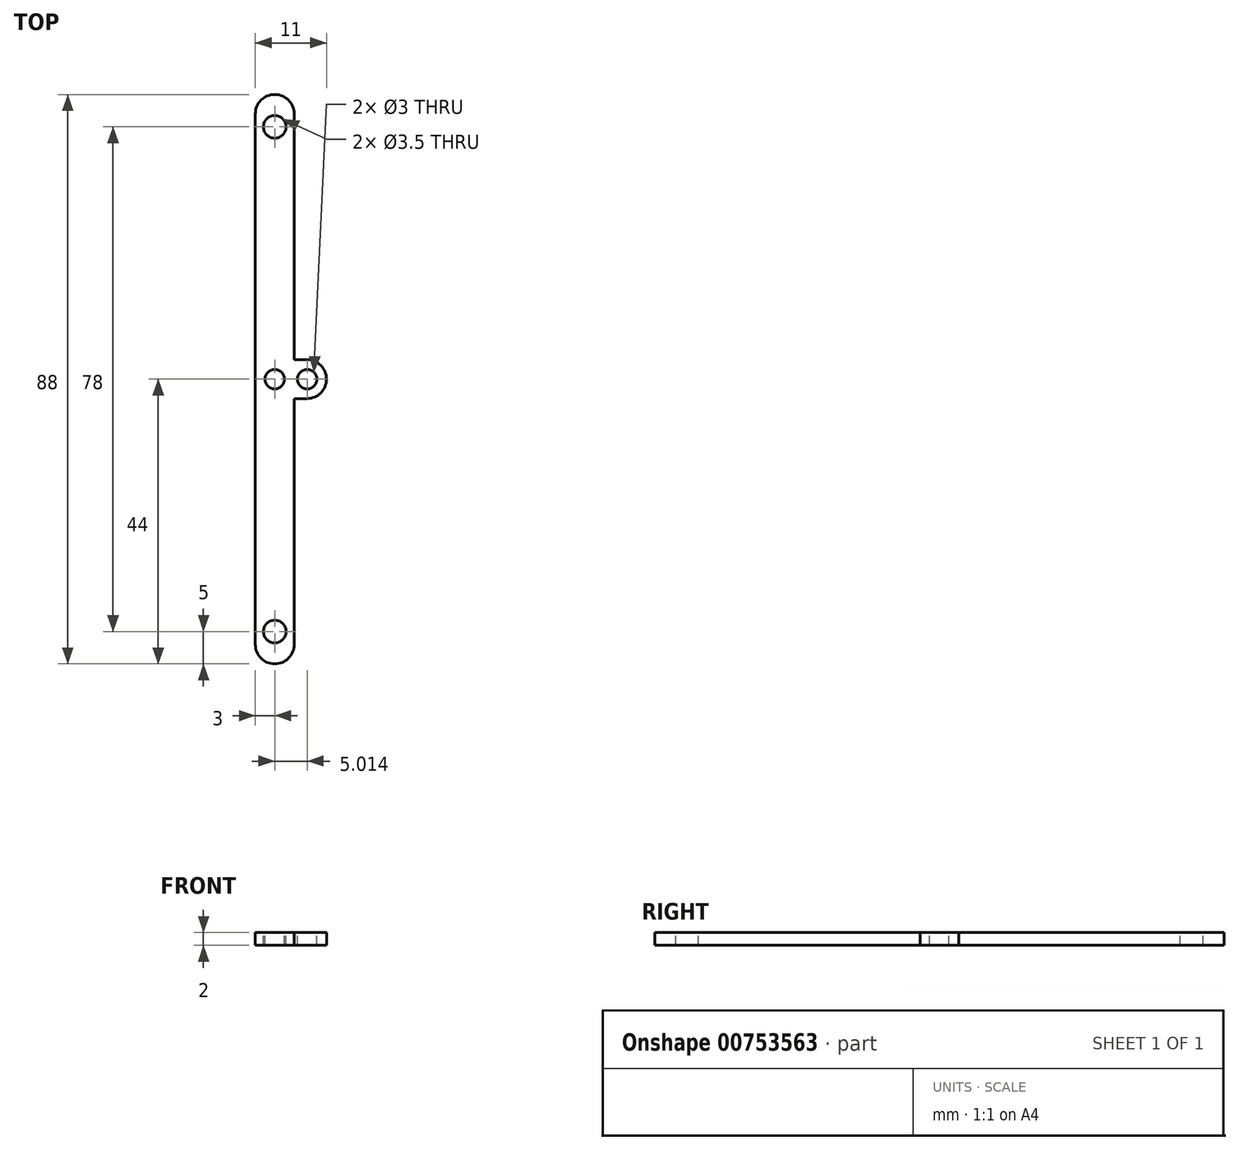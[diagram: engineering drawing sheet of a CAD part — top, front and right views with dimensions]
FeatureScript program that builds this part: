
annotation { "Feature Type Name" : "Feature", "Feature Type Description" : "" }
export const myFeature = defineFeature(function(context is Context, id is Id, definition is map)
    precondition{}
    {
        {
            var Q0;
            Q0=qCreatedBy(makeId("Top.planeOp"),FACE);
            var sketch = newSketch(context, id + "F0", { "sketchPlane" : qUnion([Q0])});
            skLineSegment(sketch, "E0.bottom", {"start": v(-3, 44) * mm, "end": v(3, 44) * mm});
            skLineSegment(sketch, "E0.top", {"start": v(-3, -44) * mm, "end": v(3, -44) * mm});
            skLineSegment(sketch, "E0.left", {"start": v(-3, 44) * mm, "end": v(-3, -44) * mm});
            skLineSegment(sketch, "E0.right", {"start": v(3, 44) * mm, "end": v(3, -44) * mm});
            skPoint(sketch, "E0.middle", {"position": v(0, 0) * mm});
            skSolve(sketch);
        }
        {
            var Q0;
            Q0 = qSketchRegion(id + "F0", true);
            extrude(context, id + "F1", {"entities" : qUnion([Q0]), "depth" : 2 * mm, "offsetDistance" : 25 * mm});
        }
        {
            var Q0;
            Q0=makeQuery(id+"F1.opExtrude","CAP_FACE",FACE,{"disambiguationData":[OSD([sQuery(id+"F0.wireOp",EDGE,"E0.bottom"),sQuery(id+"F0.wireOp",EDGE,"E0.top"),sQuery(id+"F0.wireOp",EDGE,"E0.left"),sQuery(id+"F0.wireOp",EDGE,"E0.right")])],"isStart":false});
            var sketch = newSketch(context, id + "F2", { "sketchPlane" : qUnion([Q0])});
            skCircle(sketch, "E1", {"center": v(0, 0) * mm, "radius": 1.5 * mm});
            skCircle(sketch, "E2", {"center": v(0, 39) * mm, "radius": 1.75 * mm});
            skCircle(sketch, "E3.MirrorC", {"center": v(0, -39) * mm, "radius": 1.75 * mm});
            skLineSegment(sketch, "E4", {"start": v(0, 39) * mm, "end": v(0, 44) * mm});
            skLineSegment(sketch, "E5", {"start": v(0, -44) * mm, "end": v(0, -39) * mm});
            skSolve(sketch);
        }
        {
            var Q0;
            Q0 = qSketchRegion(id + "F2", true);
            extrude(context, id + "F3", {"entities" : qUnion([Q0]), "operationType" : NewBodyOperationType.REMOVE, "endBound" : BoundingType.UP_TO_NEXT, "oppositeDirection" : true, "depth" : 25 * mm, "offsetDistance" : 25 * mm});
        }
        {
            var Q0;
            Q0=makeQuery(id+"F1.opExtrude","SWEPT_FACE",FACE,{"disambiguationData":[OSD([sQuery(id+"F0.wireOp",EDGE,"E0.right")])]});
            var sketch = newSketch(context, id + "F4", { "sketchPlane" : qUnion([Q0])});
            skLineSegment(sketch, "E6.bottom", {"start": v(0, 2) * mm, "end": v(3, 2) * mm});
            skLineSegment(sketch, "E6.top", {"start": v(0, 0) * mm, "end": v(3, 0) * mm});
            skLineSegment(sketch, "E6.right", {"start": v(3, 2) * mm, "end": v(3, 0) * mm});
            skLineSegment(sketch, "E7", {"start": v(0, 2) * mm, "end": v(-3, 2) * mm});
            skLineSegment(sketch, "E8", {"start": v(-3, 2) * mm, "end": v(-3, 0) * mm});
            skLineSegment(sketch, "E9", {"start": v(-3, 0) * mm, "end": v(0, 0) * mm});
            skSolve(sketch);
        }
        {
            var Q0;
            Q0 = qSketchRegion(id + "F4", true);
            extrude(context, id + "F5", {"entities" : qUnion([Q0]), "operationType" : NewBodyOperationType.ADD, "depth" : 5 * mm, "offsetDistance" : 25 * mm});
        }
        {
            var Q0;
            Q0=makeQuery(id+"F5.boolean.opBoolean","MERGE",FACE,{"derivedFrom":[makeQuery(id+"F1.opExtrude","CAP_FACE",FACE,{"disambiguationData":[OSD([sQuery(id+"F0.wireOp",EDGE,"E0.bottom"),sQuery(id+"F0.wireOp",EDGE,"E0.top"),sQuery(id+"F0.wireOp",EDGE,"E0.left"),sQuery(id+"F0.wireOp",EDGE,"E0.right")])],"isStart":false}),makeQuery(id+"F5.opExtrude","SWEPT_FACE",FACE,{"disambiguationData":[OSD([sQuery(id+"F4.wireOp",EDGE,"E6.bottom"),sQuery(id+"F4.wireOp",EDGE,"E7")])]})]});
            var sketch = newSketch(context, id + "F6", { "sketchPlane" : qUnion([Q0])});
            skCircle(sketch, "E10", {"center": v(5.01, 0) * mm, "radius": 1.5 * mm});
            skSolve(sketch);
        }
        {
            var Q0;
            Q0 = qSketchRegion(id + "F6", true);
            extrude(context, id + "F7", {"entities" : qUnion([Q0]), "operationType" : NewBodyOperationType.REMOVE, "endBound" : BoundingType.UP_TO_NEXT, "oppositeDirection" : true, "depth" : 25 * mm, "offsetDistance" : 25 * mm});
        }
        {
            var Q0;
            Q0=makeQuery(id+"F1.opExtrude","SWEPT_EDGE",EDGE,{"disambiguationData":[OSD([sQuery(id+"F0.wireOp",EDGE,"E0.top"),sQuery(id+"F0.wireOp",EDGE,"E0.left")])]});
            var Q1;
            Q1=makeQuery(id+"F1.opExtrude","SWEPT_EDGE",EDGE,{"disambiguationData":[OSD([sQuery(id+"F0.wireOp",EDGE,"E0.top"),sQuery(id+"F0.wireOp",EDGE,"E0.right")])]});
            var Q2;
            Q2=makeQuery(id+"F1.opExtrude","SWEPT_EDGE",EDGE,{"disambiguationData":[OSD([sQuery(id+"F0.wireOp",EDGE,"E0.bottom"),sQuery(id+"F0.wireOp",EDGE,"E0.right")])]});
            var Q3;
            Q3=makeQuery(id+"F1.opExtrude","SWEPT_EDGE",EDGE,{"disambiguationData":[OSD([sQuery(id+"F0.wireOp",EDGE,"E0.bottom"),sQuery(id+"F0.wireOp",EDGE,"E0.left")])]});
            var Q4;
            Q4=makeQuery(id+"F5.opExtrude","CAP_EDGE",EDGE,{"disambiguationData":[OSD([sQuery(id+"F4.wireOp",EDGE,"E8")])],"isStart":false});
            var Q5;
            Q5=makeQuery(id+"F5.opExtrude","CAP_EDGE",EDGE,{"disambiguationData":[OSD([sQuery(id+"F4.wireOp",EDGE,"E6.right")])],"isStart":false});
            fillet(context, id + "F8", {"entities" : qUnion([Q0, Q1, Q2, Q3, Q4, Q5]), "radius" : 3 * mm, "tangentPropagation" : true, "allowEdgeOverflow" : false});
        }
    });
